# Revit family: BAXI_PLATINUM BC_SPLIT_iMax_22_(UE)
name_source: partatom
category: Equipos mecánicos
units: mm (PartAtom-declared; Revit-internal decimal feet)

## family parameters
Compartido = No
Corte con vacíos al cargar = No
Cota de conector redondo = Diámetro de uso
Número OmniClass = 23.75.10.21
Punto de cálculo de habitación = No
Se basa en plano de trabajo = No
Siempre vertical = Sí
Tipo de pieza = Normal
Título OmniClass = Heat Pumps

## types (1)
- BAXI_PLATINUM BC_SPLIT_iMax_22_(UE)
    Altura = 1338 mm  [stored 4.38976 ft]
    Anchura = 1050 mm
    Blanco = Color RGB 216-216-216
    Cantidad compresores = 1
    Cantidad ventilador = 2
    Caudal de Aire (m3/min) = 140
    Caudal de agua (m3/h) = 3.8
    Código de montaje = 7665104
    Descripción = Platinum BC iMax
    Descrpición Articulo = PLATINUM BC iMAX 22 (UE)
    Diametro gas refrigerante = 19 mm  [stored 0.062336 ft]
    Diametro líquido refrigerante = 12.7 mm  [stored 0.0416667 ft]
    Drenaje = 32 mm  [stored 0.104987 ft]
    Fabricante = BAXI
    Gris = Color RGB 100-100-100
    Gris Oscuro = Color RGB 110-110-110
    Heating COP (kW/kW) = 3.96
    Hz = 50 Hz
    IFCExportAs = IfcPumpType
    IFCExportType = NOTDEFINED
    Intensidad máxima (A) = 19
    Modelo = PLATINUM BC iMAX 22 (UE)
    Peso (kg) = 135
    Phase = 3
    Potencia acústica dB(A) = 77
    Potencia calorifica (kW) = 21.7
    Potencia electrica absorbida (kW) = 5.48
    Profundidad = 330 mm  [stored 1.08268 ft]
    Revit Version = 2016
    Rojo = Color RGB 255-000-000
    Tipo Articulo = PLATINUM BC iMAX 22 (UE)
    Tipo Ventilador = Propeller Fan
    Tipo compresor = Inverter hermetic scroll
    Tipo refrigerante = R410A
    URL = https://www.baxi.es
    URL PRODUCT = https://www.baxi.es
    Voltage = 400 V

note: [stored X ft] marks values corroborated as IEEE doubles in the binary element streams (Revit-internal decimal feet)

## geometry (parser evidence)
native form markers: Blend x2, Sweep x9
no freeform markers — native parametric forms only
